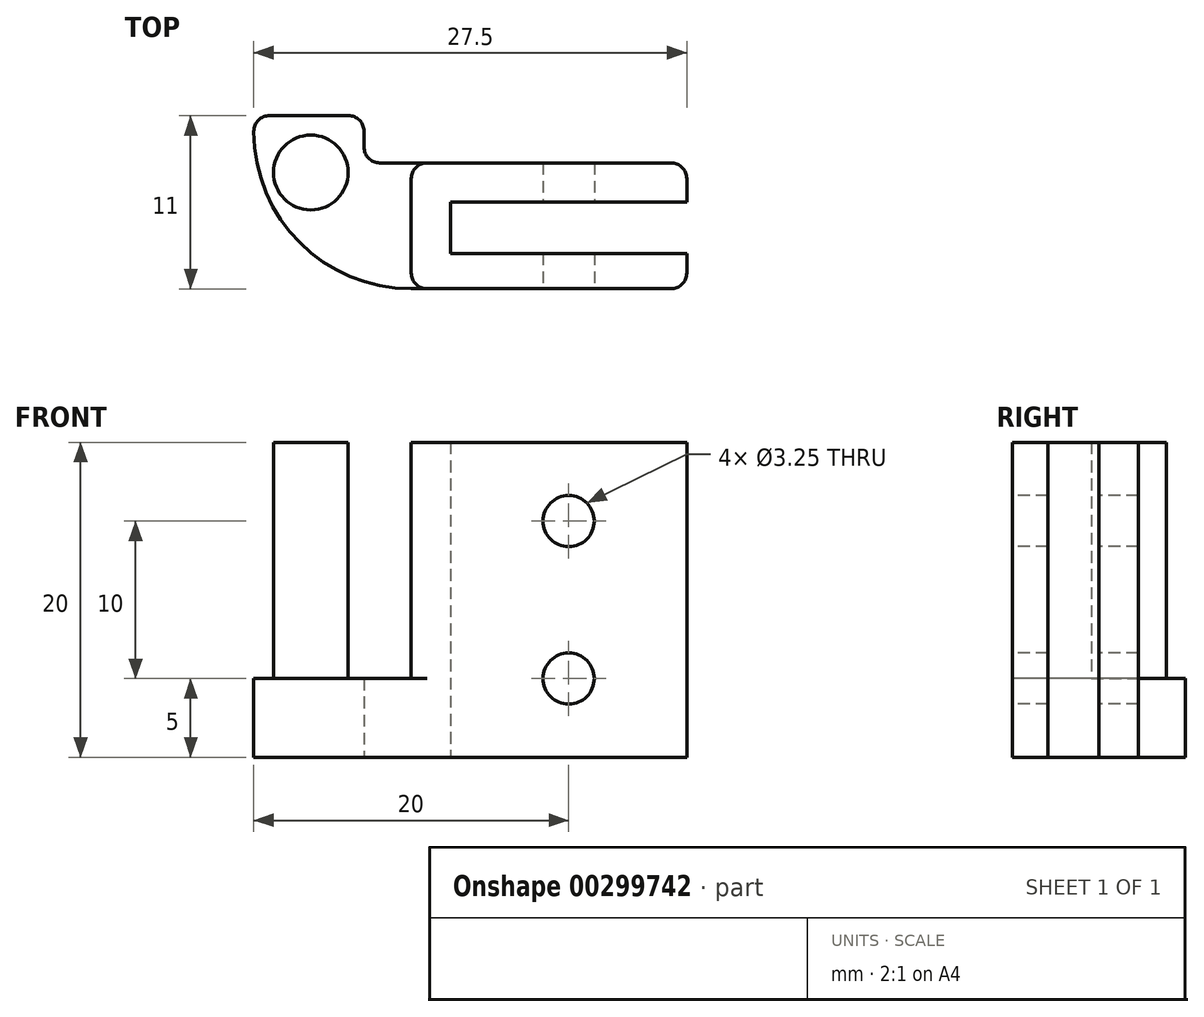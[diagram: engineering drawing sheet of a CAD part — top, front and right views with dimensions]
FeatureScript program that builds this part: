
annotation { "Feature Type Name" : "Feature", "Feature Type Description" : "" }
export const myFeature = defineFeature(function(context is Context, id is Id, definition is map)
    precondition{}
    {
        {
            var Q0;
            Q0=qCreatedBy(makeId("Top.planeOp"),FACE);
            var sketch = newSketch(context, id + "F0", { "sketchPlane" : qUnion([Q0])});
            skLineSegment(sketch, "E0.bottom", {"start": v(7.5, -1.63) * mm, "end": v(-7.5, -1.63) * mm});
            skLineSegment(sketch, "E0.top", {"start": v(7.5, 1.62) * mm, "end": v(-7.5, 1.62) * mm});
            skLineSegment(sketch, "E0.right", {"start": v(-7.5, -1.63) * mm, "end": v(-7.5, 1.63) * mm});
            skPoint(sketch, "E0.middle", {"position": v(0, 0) * mm});
            skLineSegment(sketch, "E1", {"start": v(7.5, 1.63) * mm, "end": v(7.5, 4.13) * mm});
            skLineSegment(sketch, "E2", {"start": v(7.5, 4.13) * mm, "end": v(-10, 4.12) * mm});
            skLineSegment(sketch, "E3", {"start": v(-10, 4.12) * mm, "end": v(-10, -3.88) * mm});
            skLineSegment(sketch, "E4", {"start": v(-10, -3.88) * mm, "end": v(7.5, -3.87) * mm});
            skLineSegment(sketch, "E5", {"start": v(7.5, -3.87) * mm, "end": v(7.5, -1.63) * mm});
            skLineSegment(sketch, "E6", {"start": v(-20, 7.12) * mm, "end": v(-20, -3.88) * mm});
            skLineSegment(sketch, "E7", {"start": v(-20, -3.88) * mm, "end": v(-10, -3.88) * mm});
            skCircle(sketch, "E8", {"center": v(-16.38, 3.51) * mm, "radius": 2.38 * mm});
            skLineSegment(sketch, "E9", {"start": v(-10, 4.12) * mm, "end": v(-13, 4.12) * mm});
            skLineSegment(sketch, "E10", {"start": v(-13, 4.12) * mm, "end": v(-13, 7.12) * mm});
            skLineSegment(sketch, "E11", {"start": v(-13, 7.12) * mm, "end": v(-20, 7.12) * mm});
            skSolve(sketch);
        }
        {
            var Q0;
            Q0=makeQuery(id+"F0.imprint","IMPRINT",FACE,{"disambiguationData":[TD([[makeQuery(id+"F0.imprint","IMPRINT",EDGE,{"derivedFrom":sQuery(id+"F0.wireOp",EDGE,"E0.bottom")}),1.0]])]});
            extrude(context, id + "F1", {"entities" : qUnion([Q0]), "depth" : 20 * mm});
        }
        {
            var Q0;
            Q0=makeQuery(id+"F0.imprint","IMPRINT",FACE,{"disambiguationData":[TD([[makeQuery(id+"F0.imprint","IMPRINT",EDGE,{"derivedFrom":sQuery(id+"F0.wireOp",EDGE,"E3")}),-1.0]])]});
            extrude(context, id + "F2", {"entities" : qUnion([Q0]), "operationType" : NewBodyOperationType.ADD, "depth" : 5 * mm});
        }
        {
            var Q0;
            Q0=makeQuery(id+"F0.imprint","IMPRINT",FACE,{"disambiguationData":[TD([[makeQuery(id+"F0.imprint","IMPRINT",EDGE,{"derivedFrom":sQuery(id+"F0.wireOp",EDGE,"E8")}),1.0]])]});
            extrude(context, id + "F3", {"entities" : qUnion([Q0]), "operationType" : NewBodyOperationType.ADD, "depth" : 20 * mm});
        }
        {
            var Q0;
            Q0=makeQuery(id+"F2.opExtrude","SWEPT_EDGE",EDGE,{"disambiguationData":[OSD([sQuery(id+"F0.wireOp",EDGE,"E6"),sQuery(id+"F0.wireOp",EDGE,"E11")])]});
            var Q1;
            Q1=makeQuery(id+"F1.opExtrude","SWEPT_EDGE",EDGE,{"disambiguationData":[OSD([sQuery(id+"F0.wireOp",EDGE,"E1"),sQuery(id+"F0.wireOp",EDGE,"E2")])]});
            var Q2;
            Q2=makeQuery(id+"F1.opExtrude","SWEPT_EDGE",EDGE,{"disambiguationData":[OSD([sQuery(id+"F0.wireOp",EDGE,"E4"),sQuery(id+"F0.wireOp",EDGE,"E5")])]});
            var Q3;
            Q3=makeQuery(id+"F1.opExtrude","SWEPT_EDGE",EDGE,{"disambiguationData":[OSD([sQuery(id+"F0.wireOp",EDGE,"E2"),sQuery(id+"F0.wireOp",EDGE,"E3"),sQuery(id+"F0.wireOp",EDGE,"E9")])]});
            var Q4;
            Q4=makeQuery(id+"F1.opExtrude","SWEPT_EDGE",EDGE,{"disambiguationData":[OSD([sQuery(id+"F0.wireOp",EDGE,"E3"),sQuery(id+"F0.wireOp",EDGE,"E4"),sQuery(id+"F0.wireOp",EDGE,"E7")])]});
            var Q5;
            Q5=makeQuery(id+"F2.opExtrude","SWEPT_EDGE",EDGE,{"disambiguationData":[OSD([sQuery(id+"F0.wireOp",EDGE,"E10"),sQuery(id+"F0.wireOp",EDGE,"E11")])]});
            var Q6;
            Q6=makeQuery(id+"F2.opExtrude","SWEPT_EDGE",EDGE,{"disambiguationData":[OSD([sQuery(id+"F0.wireOp",EDGE,"E9"),sQuery(id+"F0.wireOp",EDGE,"E10")])]});
            fillet(context, id + "F4", {"entities" : qUnion([Q0, Q1, Q2, Q3, Q4, Q5, Q6]), "radius" : 1 * mm, "tangentPropagation" : true, "allowEdgeOverflow" : false});
        }
        {
            var Q0;
            Q0=makeQuery(id+"F2.boolean.opBoolean","MERGE",FACE,{"derivedFrom":[makeQuery(id+"F1.opExtrude","SWEPT_FACE",FACE,{"disambiguationData":[OSD([sQuery(id+"F0.wireOp",EDGE,"E4")])]}),makeQuery(id+"F2.opExtrude","SWEPT_FACE",FACE,{"disambiguationData":[OSD([sQuery(id+"F0.wireOp",EDGE,"E7")])]})]});
            var sketch = newSketch(context, id + "F5", { "sketchPlane" : qUnion([Q0])});
            skLineSegment(sketch, "E12", {"start": v(0, 20) * mm, "end": v(0, 15) * mm});
            skLineSegment(sketch, "E13", {"start": v(0, 0) * mm, "end": v(0, 5) * mm});
            skCircle(sketch, "E14", {"center": v(0, 15) * mm, "radius": 1.63 * mm});
            skCircle(sketch, "E15", {"center": v(0, 5) * mm, "radius": 1.63 * mm});
            skSolve(sketch);
        }
        {
            var Q0;
            Q0=makeQuery(id+"F5.imprint","IMPRINT",FACE,{"disambiguationData":[TD([[makeQuery(id+"F5.imprint","IMPRINT",EDGE,{"derivedFrom":sQuery(id+"F5.wireOp",EDGE,"E14")}),1.0]])]});
            var Q1;
            Q1=makeQuery(id+"F5.imprint","IMPRINT",FACE,{"disambiguationData":[TD([[makeQuery(id+"F5.imprint","IMPRINT",EDGE,{"derivedFrom":sQuery(id+"F5.wireOp",EDGE,"E15")}),1.0]])]});
            extrude(context, id + "F6", {"entities" : qUnion([Q0, Q1]), "operationType" : NewBodyOperationType.REMOVE, "oppositeDirection" : true, "depth" : 8.5 * mm});
        }
        {
            var Q0;
            Q0=makeQuery(id+"F2.opExtrude","SWEPT_EDGE",EDGE,{"disambiguationData":[OSD([sQuery(id+"F0.wireOp",EDGE,"E6"),sQuery(id+"F0.wireOp",EDGE,"E7")])]});
            fillet(context, id + "F7", {"entities" : qUnion([Q0]), "radius" : 10 * mm, "tangentPropagation" : true, "allowEdgeOverflow" : false});
        }
    });
